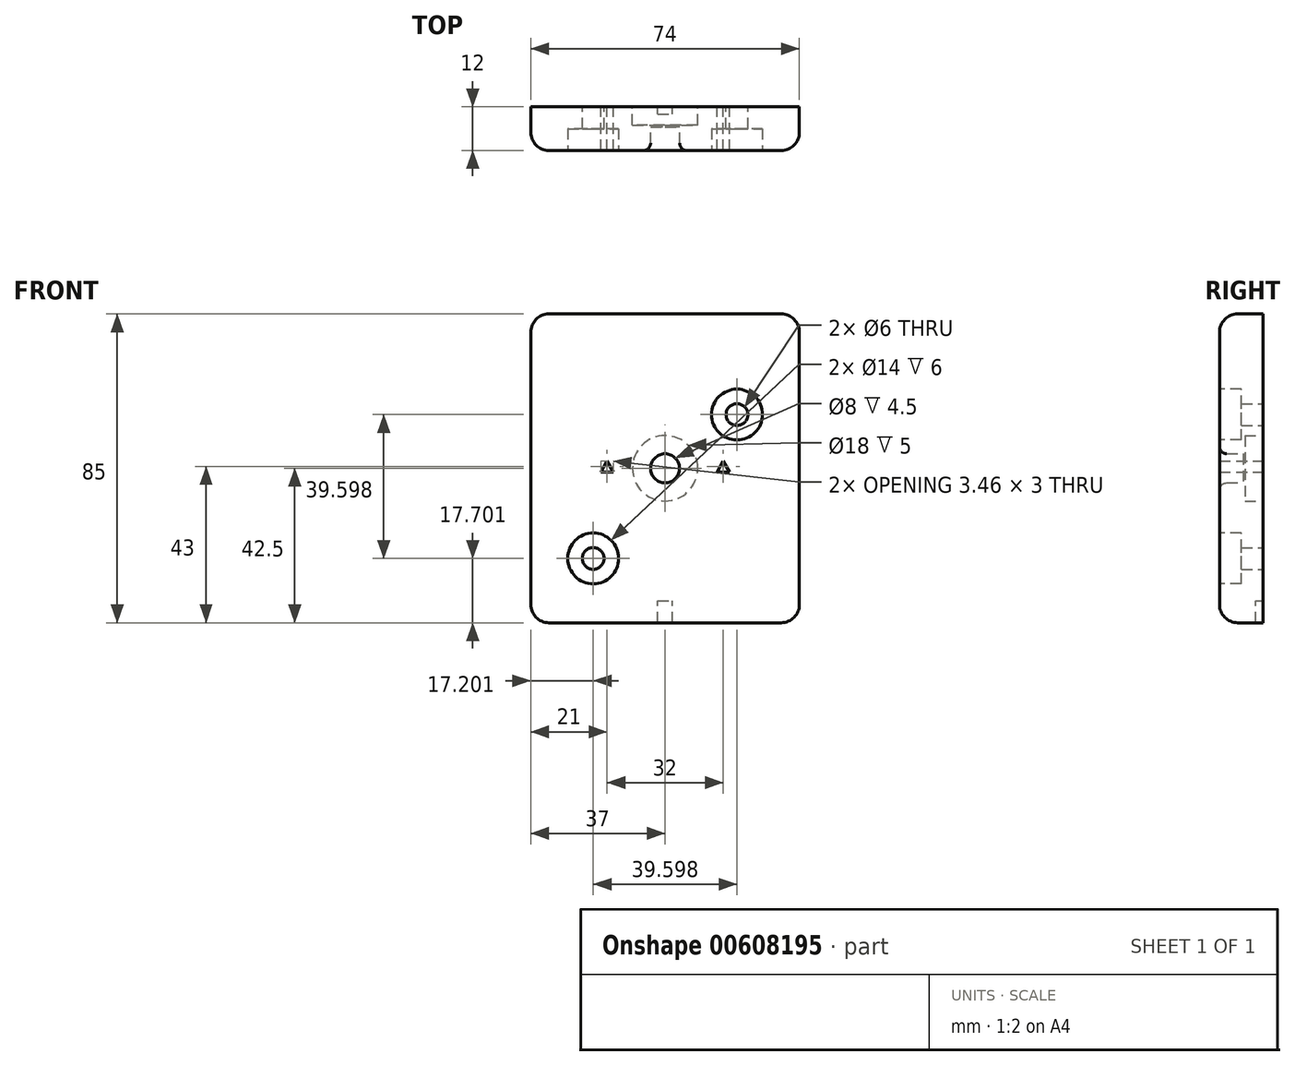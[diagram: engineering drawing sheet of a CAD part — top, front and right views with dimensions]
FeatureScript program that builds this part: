
annotation { "Feature Type Name" : "Feature", "Feature Type Description" : "" }
export const myFeature = defineFeature(function(context is Context, id is Id, definition is map)
    precondition{}
    {
        {
            var Q0;
            Q0=qCreatedBy(makeId("Front.planeOp"),FACE);
            var sketch = newSketch(context, id + "F0", { "sketchPlane" : qUnion([Q0])});
            skLineSegment(sketch, "E0.bottom", {"start": v(37, -42.5) * mm, "end": v(-37, -42.5) * mm});
            skLineSegment(sketch, "E0.top", {"start": v(37, 42.5) * mm, "end": v(-37, 42.5) * mm});
            skLineSegment(sketch, "E0.left", {"start": v(37, -42.5) * mm, "end": v(37, 42.5) * mm});
            skLineSegment(sketch, "E0.right", {"start": v(-37, -42.5) * mm, "end": v(-37, 42.5) * mm});
            skPoint(sketch, "E0.middle", {"position": v(0, 0) * mm});
            skLineSegment(sketch, "E1.bottom", {"start": v(31.5, 37.5) * mm, "end": v(-31.5, 37.5) * mm, "construction": true});
            skLineSegment(sketch, "E1.top", {"start": v(31.5, -37.5) * mm, "end": v(-31.5, -37.5) * mm, "construction": true});
            skLineSegment(sketch, "E1.left", {"start": v(31.5, 37.5) * mm, "end": v(31.5, -37.5) * mm, "construction": true});
            skLineSegment(sketch, "E1.right", {"start": v(-31.5, 37.5) * mm, "end": v(-31.5, -37.5) * mm, "construction": true});
            skCircle(sketch, "E2", {"center": v(0, 0) * mm, "radius": 4 * mm});
            skCircle(sketch, "E3.cCircle", {"center": v(-16, 0) * mm, "radius": 1 * mm, "construction": true});
            skLineSegment(sketch, "E3.0", {"start": v(-16, 2) * mm, "end": v(-14.27, -1) * mm});
            skLineSegment(sketch, "E3.1", {"start": v(-14.27, -1) * mm, "end": v(-17.73, -1) * mm});
            skLineSegment(sketch, "E3.2", {"start": v(-17.73, -1) * mm, "end": v(-16, 2) * mm});
            skPoint(sketch, "E3.0.midPoint", {"position": v(-15.13, 0.5) * mm});
            skCircle(sketch, "E4.cCircle", {"center": v(16, 0) * mm, "radius": 1 * mm, "construction": true});
            skLineSegment(sketch, "E4.0", {"start": v(16, 2) * mm, "end": v(17.73, -1) * mm});
            skLineSegment(sketch, "E4.1", {"start": v(17.73, -1) * mm, "end": v(14.27, -1) * mm});
            skLineSegment(sketch, "E4.2", {"start": v(14.27, -1) * mm, "end": v(16, 2) * mm});
            skPoint(sketch, "E4.0.midPoint", {"position": v(16.87, 0.5) * mm});
            skLineSegment(sketch, "E5", {"start": v(38.39, 33.39) * mm, "end": v(-38.39, -43.39) * mm, "construction": true});
            skCircle(sketch, "E6", {"center": v(19.8, 14.8) * mm, "radius": 3 * mm});
            skCircle(sketch, "E7", {"center": v(-19.8, -24.8) * mm, "radius": 3 * mm});
            skPoint(sketch, "E8", {"position": v(0, -5) * mm});
            skSolve(sketch);
        }
        {
            var Q0;
            Q0 = qSketchRegion(id + "F0", true);
            extrude(context, id + "F1", {"entities" : qUnion([Q0]), "depth" : 12 * mm, "offsetDistance" : 25 * mm});
        }
        {
            var Q0;
            Q0=makeQuery(id+"F1.opExtrude","CAP_FACE",FACE,{"disambiguationData":[OSD([sQuery(id+"F0.wireOp",EDGE,"E0.bottom"),sQuery(id+"F0.wireOp",EDGE,"E0.top"),sQuery(id+"F0.wireOp",EDGE,"E0.left"),sQuery(id+"F0.wireOp",EDGE,"E0.right"),sQuery(id+"F0.wireOp",EDGE,"E2"),sQuery(id+"F0.wireOp",EDGE,"E3.0"),sQuery(id+"F0.wireOp",EDGE,"E3.1"),sQuery(id+"F0.wireOp",EDGE,"E3.2"),sQuery(id+"F0.wireOp",EDGE,"E4.0"),sQuery(id+"F0.wireOp",EDGE,"E4.1"),sQuery(id+"F0.wireOp",EDGE,"E4.2"),sQuery(id+"F0.wireOp",EDGE,"E6"),sQuery(id+"F0.wireOp",EDGE,"E7")])],"isStart":false});
            var sketch = newSketch(context, id + "F2", { "sketchPlane" : qUnion([Q0])});
            skCircle(sketch, "E9.0", {"center": v(19.8, 14.8) * mm, "radius": 7 * mm});
            skCircle(sketch, "E10.0", {"center": v(-19.8, -24.8) * mm, "radius": 7 * mm});
            skSolve(sketch);
        }
        {
            var Q0;
            Q0 = qSketchRegion(id + "F2", true);
            extrude(context, id + "F3", {"entities" : qUnion([Q0]), "operationType" : NewBodyOperationType.REMOVE, "oppositeDirection" : true, "depth" : 6 * mm, "offsetDistance" : 25 * mm});
        }
        {
            var Q0;
            Q0=qCreatedBy(makeId("Right.planeOp"),FACE);
            var sketch = newSketch(context, id + "F4", { "sketchPlane" : qUnion([Q0])});
            skLineSegment(sketch, "E11.0", {"start": v(-2, -42.5) * mm, "end": v(0, -42.5) * mm});
            skLineSegment(sketch, "E12.0", {"start": v(0, -42.5) * mm, "end": v(0, -36.5) * mm});
            skLineSegment(sketch, "E13", {"start": v(-2, -42.5) * mm, "end": v(-2, -36.5) * mm});
            skLineSegment(sketch, "E14", {"start": v(-2, -36.5) * mm, "end": v(0, -36.5) * mm});
            skPoint(sketch, "E15.orphan", {"position": v(-12, -42.5) * mm});
            skPoint(sketch, "E16.orphan", {"position": v(0, 42.5) * mm});
            skSolve(sketch);
        }
        {
            var Q0;
            Q0 = qSketchRegion(id + "F4", true);
            extrude(context, id + "F5", {"entities" : qUnion([Q0]), "operationType" : NewBodyOperationType.REMOVE, "oppositeDirection" : true, "depth" : 4 * mm, "offsetDistance" : 25 * mm, "symmetric" : true});
        }
        {
            var Q0;
            Q0=makeQuery(id+"F1.opExtrude","CAP_FACE",FACE,{"disambiguationData":[OSD([sQuery(id+"F0.wireOp",EDGE,"E0.bottom"),sQuery(id+"F0.wireOp",EDGE,"E0.top"),sQuery(id+"F0.wireOp",EDGE,"E0.left"),sQuery(id+"F0.wireOp",EDGE,"E0.right"),sQuery(id+"F0.wireOp",EDGE,"E2"),sQuery(id+"F0.wireOp",EDGE,"E3.0"),sQuery(id+"F0.wireOp",EDGE,"E3.1"),sQuery(id+"F0.wireOp",EDGE,"E3.2"),sQuery(id+"F0.wireOp",EDGE,"E4.0"),sQuery(id+"F0.wireOp",EDGE,"E4.1"),sQuery(id+"F0.wireOp",EDGE,"E4.2"),sQuery(id+"F0.wireOp",EDGE,"E6"),sQuery(id+"F0.wireOp",EDGE,"E7")])],"isStart":true});
            var sketch = newSketch(context, id + "F6", { "sketchPlane" : qUnion([Q0])});
            skCircle(sketch, "E17.0", {"center": v(0, 0) * mm, "radius": 9 * mm});
            skSolve(sketch);
        }
        {
            var Q0;
            Q0 = qSketchRegion(id + "F6", true);
            extrude(context, id + "F7", {"entities" : qUnion([Q0]), "operationType" : NewBodyOperationType.REMOVE, "oppositeDirection" : true, "depth" : 5 * mm, "offsetDistance" : 25 * mm});
        }
        {
            var Q0;
            Q0=makeQuery(id+"F7.boolean.opBoolean","COPY",FACE,{"derivedFrom":makeQuery(id+"F7.opExtrude","CAP_FACE",FACE,{"disambiguationData":[OSD([sQuery(id+"F6.wireOp",EDGE,"E17.0")])],"isStart":false})});
            var sketch = newSketch(context, id + "F8", { "sketchPlane" : qUnion([Q0])});
            skCircle(sketch, "E18.0", {"center": v(0, 0) * mm, "radius": 4 * mm});
            skSolve(sketch);
        }
        {
            var Q0;
            Q0 = qSketchRegion(id + "F8", true);
            extrude(context, id + "F9", {"entities" : qUnion([Q0]), "operationType" : NewBodyOperationType.ADD, "oppositeDirection" : true, "depth" : 0.5 * mm, "offsetDistance" : 25 * mm});
        }
        {
            var Q0;
            Q0=makeQuery(id+"F1.opExtrude","CAP_EDGE",EDGE,{"disambiguationData":[OSD([sQuery(id+"F0.wireOp",EDGE,"E0.top")])],"isStart":false});
            var Q1;
            Q1=makeQuery(id+"F1.opExtrude","CAP_EDGE",EDGE,{"disambiguationData":[OSD([sQuery(id+"F0.wireOp",EDGE,"E0.right")])],"isStart":false});
            var Q2;
            Q2=makeQuery(id+"F1.opExtrude","CAP_EDGE",EDGE,{"disambiguationData":[OSD([sQuery(id+"F0.wireOp",EDGE,"E0.left")])],"isStart":false});
            var Q3;
            Q3=makeQuery(id+"F1.opExtrude","CAP_EDGE",EDGE,{"disambiguationData":[OSD([sQuery(id+"F0.wireOp",EDGE,"E0.bottom")])],"isStart":false});
            var Q4;
            Q4=makeQuery(id+"F1.opExtrude","SWEPT_EDGE",EDGE,{"disambiguationData":[OSD([sQuery(id+"F0.wireOp",EDGE,"E0.bottom"),sQuery(id+"F0.wireOp",EDGE,"E0.left")])]});
            var Q5;
            Q5=makeQuery(id+"F1.opExtrude","SWEPT_EDGE",EDGE,{"disambiguationData":[OSD([sQuery(id+"F0.wireOp",EDGE,"E0.top"),sQuery(id+"F0.wireOp",EDGE,"E0.left")])]});
            var Q6;
            Q6=makeQuery(id+"F1.opExtrude","SWEPT_EDGE",EDGE,{"disambiguationData":[OSD([sQuery(id+"F0.wireOp",EDGE,"E0.top"),sQuery(id+"F0.wireOp",EDGE,"E0.right")])]});
            var Q7;
            Q7=makeQuery(id+"F1.opExtrude","SWEPT_EDGE",EDGE,{"disambiguationData":[OSD([sQuery(id+"F0.wireOp",EDGE,"E0.bottom"),sQuery(id+"F0.wireOp",EDGE,"E0.right")])]});
            fillet(context, id + "F10", {"entities" : qUnion([Q0, Q1, Q2, Q3, Q4, Q5, Q6, Q7]), "radius" : 5 * mm, "tangentPropagation" : true, "allowEdgeOverflow" : false});
        }
        {
            var Q0;
            Q0=makeQuery(id+"F7.boolean.opBoolean","COPY",EDGE,{"derivedFrom":makeQuery(id+"F7.opExtrude","CAP_EDGE",EDGE,{"disambiguationData":[OSD([sQuery(id+"F6.wireOp",EDGE,"E17.0")])],"isStart":true})});
            var Q1;
            Q1=makeQuery(id+"F1.opExtrude","CAP_EDGE",EDGE,{"disambiguationData":[OSD([sQuery(id+"F0.wireOp",EDGE,"E2")])],"isStart":false});
            fillet(context, id + "F11", {"entities" : qUnion([Q0, Q1]), "radius" : 2 * mm, "tangentPropagation" : true, "allowEdgeOverflow" : false});
        }
    });
